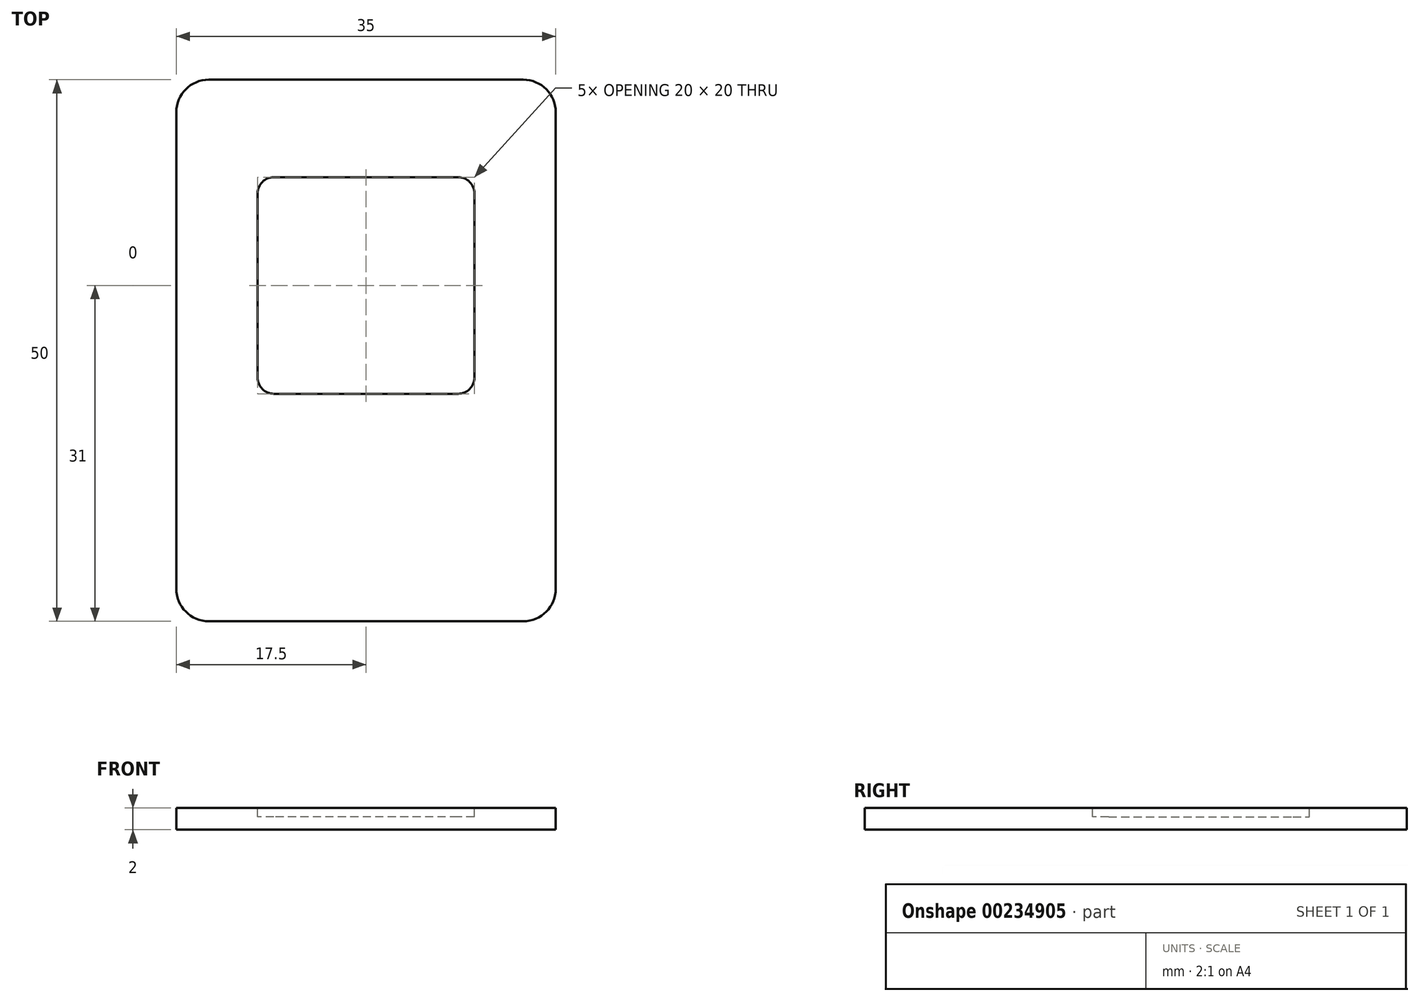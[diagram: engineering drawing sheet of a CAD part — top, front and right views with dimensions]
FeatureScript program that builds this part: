
annotation { "Feature Type Name" : "Feature", "Feature Type Description" : "" }
export const myFeature = defineFeature(function(context is Context, id is Id, definition is map)
    precondition{}
    {
        {
            var Q0;
            Q0=qCreatedBy(makeId("Top.planeOp"),FACE);
            var sketch = newSketch(context, id + "F0", { "sketchPlane" : qUnion([Q0])});
            skLineSegment(sketch, "E0.bottom", {"start": v(14.5, 25) * mm, "end": v(-14.5, 25) * mm});
            skLineSegment(sketch, "E0.top", {"start": v(14.5, -25) * mm, "end": v(-14.5, -25) * mm});
            skLineSegment(sketch, "E0.left", {"start": v(17.5, 22) * mm, "end": v(17.5, -22) * mm});
            skLineSegment(sketch, "E0.right", {"start": v(-17.5, 22) * mm, "end": v(-17.5, -22) * mm});
            skPoint(sketch, "E0.middle", {"position": v(0, 0) * mm});
            skPoint(sketch, "E1.visualSharp", {"position": v(-17.5, 25) * mm});
            skArc(sketch, "E1.filletArc", {"start": v(-14.5, 25) * mm, "mid": v(-16.62, 24.12) * mm, "end": v(-17.5, 22) * mm});
            skPoint(sketch, "E2.visualSharp", {"position": v(17.5, 25) * mm});
            skArc(sketch, "E2.filletArc", {"start": v(17.5, 22) * mm, "mid": v(16.62, 24.12) * mm, "end": v(14.5, 25) * mm});
            skPoint(sketch, "E3.visualSharp", {"position": v(17.5, -25) * mm});
            skArc(sketch, "E3.filletArc", {"start": v(14.5, -25) * mm, "mid": v(16.62, -24.12) * mm, "end": v(17.5, -22) * mm});
            skPoint(sketch, "E4.visualSharp", {"position": v(-17.5, -25) * mm});
            skArc(sketch, "E4.filletArc", {"start": v(-17.5, -22) * mm, "mid": v(-16.62, -24.12) * mm, "end": v(-14.5, -25) * mm});
            skSolve(sketch);
        }
        {
            var Q0;
            Q0=makeQuery(id+"F0.imprint","IMPRINT",FACE,{"disambiguationData":[TD([[makeQuery(id+"F0.imprint","IMPRINT",EDGE,{"derivedFrom":sQuery(id+"F0.wireOp",EDGE,"E0.bottom")}),1.0]])]});
            extrude(context, id + "F1", {"entities" : qUnion([Q0]), "depth" : 2 * mm});
        }
        {
            var Q0;
            Q0=makeQuery(id+"F1.opExtrude","CAP_FACE",FACE,{"disambiguationData":[OSD([sQuery(id+"F0.wireOp",EDGE,"E0.bottom"),sQuery(id+"F0.wireOp",EDGE,"E0.top"),sQuery(id+"F0.wireOp",EDGE,"E0.left"),sQuery(id+"F0.wireOp",EDGE,"E0.right"),sQuery(id+"F0.wireOp",EDGE,"E1.filletArc"),sQuery(id+"F0.wireOp",EDGE,"E2.filletArc"),sQuery(id+"F0.wireOp",EDGE,"E3.filletArc"),sQuery(id+"F0.wireOp",EDGE,"E4.filletArc")])],"isStart":false});
            var sketch = newSketch(context, id + "F2", { "sketchPlane" : qUnion([Q0])});
            skLineSegment(sketch, "E5.bottom", {"start": v(8.5, -4) * mm, "end": v(-8.5, -4) * mm});
            skLineSegment(sketch, "E5.top", {"start": v(8.5, 16) * mm, "end": v(-8.5, 16) * mm});
            skLineSegment(sketch, "E5.left", {"start": v(10, -2.5) * mm, "end": v(10, 14.5) * mm});
            skLineSegment(sketch, "E5.right", {"start": v(-10, -2.5) * mm, "end": v(-10, 14.5) * mm});
            skPoint(sketch, "E5.middle", {"position": v(0, 6) * mm});
            skPoint(sketch, "E6.visualSharp", {"position": v(-10, 16) * mm});
            skArc(sketch, "E6.filletArc", {"start": v(-8.5, 16) * mm, "mid": v(-9.56, 15.56) * mm, "end": v(-10, 14.5) * mm});
            skPoint(sketch, "E7.visualSharp", {"position": v(10, 16) * mm});
            skArc(sketch, "E7.filletArc", {"start": v(10, 14.5) * mm, "mid": v(9.56, 15.56) * mm, "end": v(8.5, 16) * mm});
            skPoint(sketch, "E8.visualSharp", {"position": v(10, -4) * mm});
            skArc(sketch, "E8.filletArc", {"start": v(8.5, -4) * mm, "mid": v(9.56, -3.56) * mm, "end": v(10, -2.5) * mm});
            skPoint(sketch, "E9.visualSharp", {"position": v(-10, -4) * mm});
            skArc(sketch, "E9.filletArc", {"start": v(-10, -2.5) * mm, "mid": v(-9.56, -3.56) * mm, "end": v(-8.5, -4) * mm});
            skSolve(sketch);
        }
        {
            var Q0;
            Q0=makeQuery(id+"F2.imprint","IMPRINT",FACE,{"disambiguationData":[TD([[makeQuery(id+"F2.imprint","IMPRINT",EDGE,{"derivedFrom":sQuery(id+"F2.wireOp",EDGE,"E5.bottom")}),-1.0]])]});
            extrude(context, id + "F3", {"entities" : qUnion([Q0]), "operationType" : NewBodyOperationType.REMOVE, "oppositeDirection" : true, "depth" : 0.8 * mm});
        }
    });
